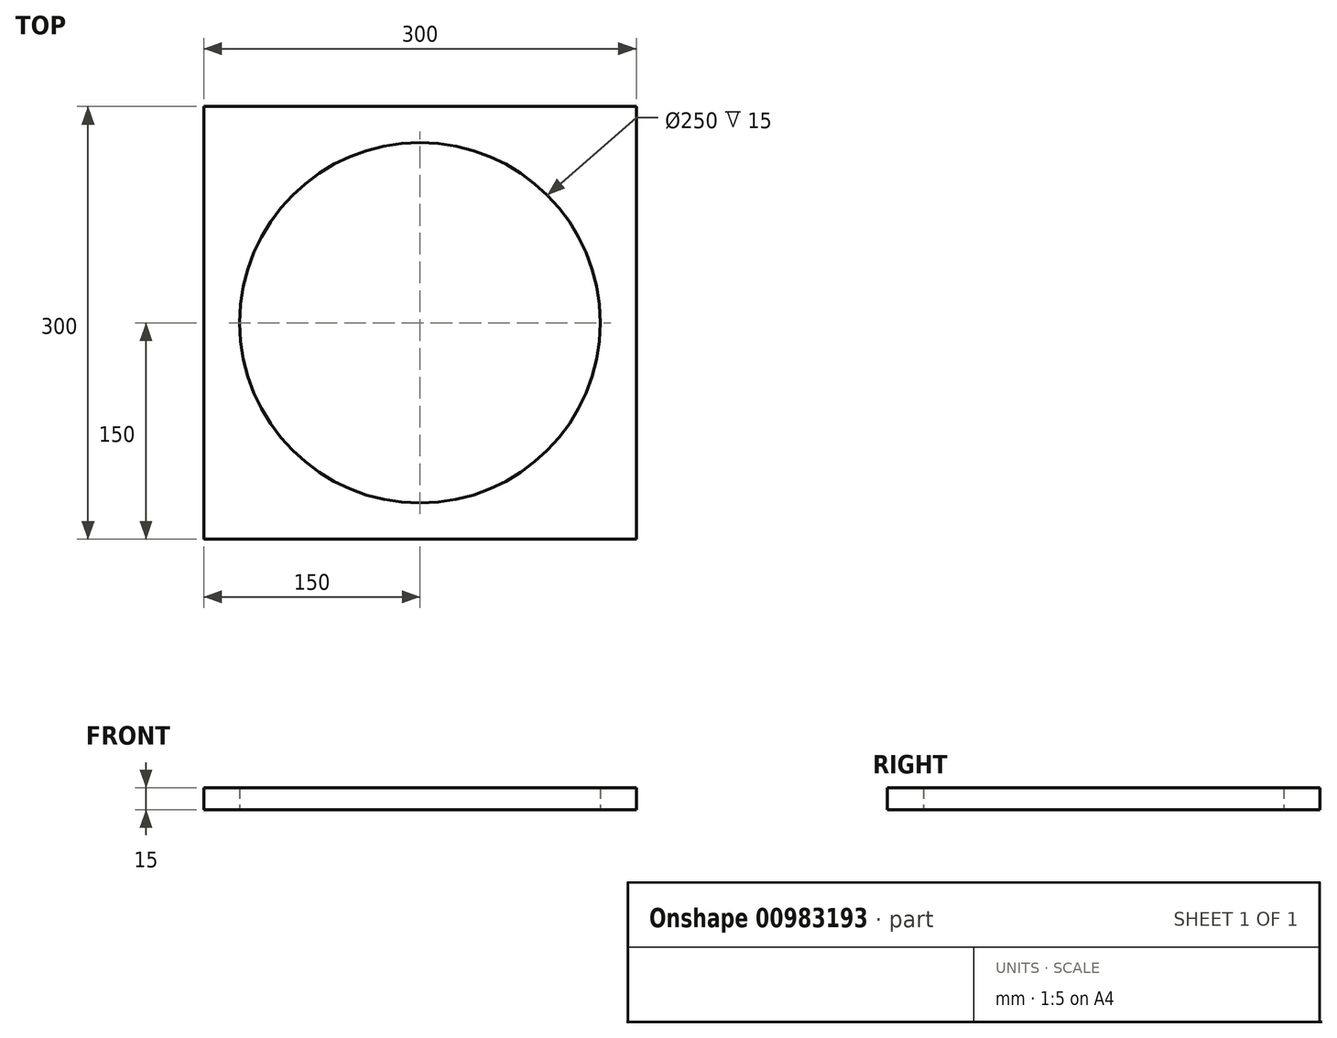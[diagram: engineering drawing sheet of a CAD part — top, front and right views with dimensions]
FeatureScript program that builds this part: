
annotation { "Feature Type Name" : "Feature", "Feature Type Description" : "" }
export const myFeature = defineFeature(function(context is Context, id is Id, definition is map)
    precondition{}
    {
        {
            var Q0;
            Q0=qCreatedBy(makeId("Top.planeOp"),FACE);
            var sketch = newSketch(context, id + "F0", { "sketchPlane" : qUnion([Q0])});
            skLineSegment(sketch, "E0.bottom", {"start": v(150, 150) * mm, "end": v(-150, 150) * mm});
            skLineSegment(sketch, "E0.top", {"start": v(150, -150) * mm, "end": v(-150, -150) * mm});
            skLineSegment(sketch, "E0.left", {"start": v(150, 150) * mm, "end": v(150, -150) * mm});
            skLineSegment(sketch, "E0.right", {"start": v(-150, 150) * mm, "end": v(-150, -150) * mm});
            skPoint(sketch, "E0.middle", {"position": v(0, 0) * mm});
            skCircle(sketch, "E1", {"center": v(0, 0) * mm, "radius": 125 * mm});
            skSolve(sketch);
        }
        {
            var Q0;
            Q0 = qSketchRegion(id + "F0", true);
            extrude(context, id + "F1", {"entities" : qUnion([Q0]), "depth" : 15 * mm, "offsetDistance" : 25 * mm});
        }
    });
